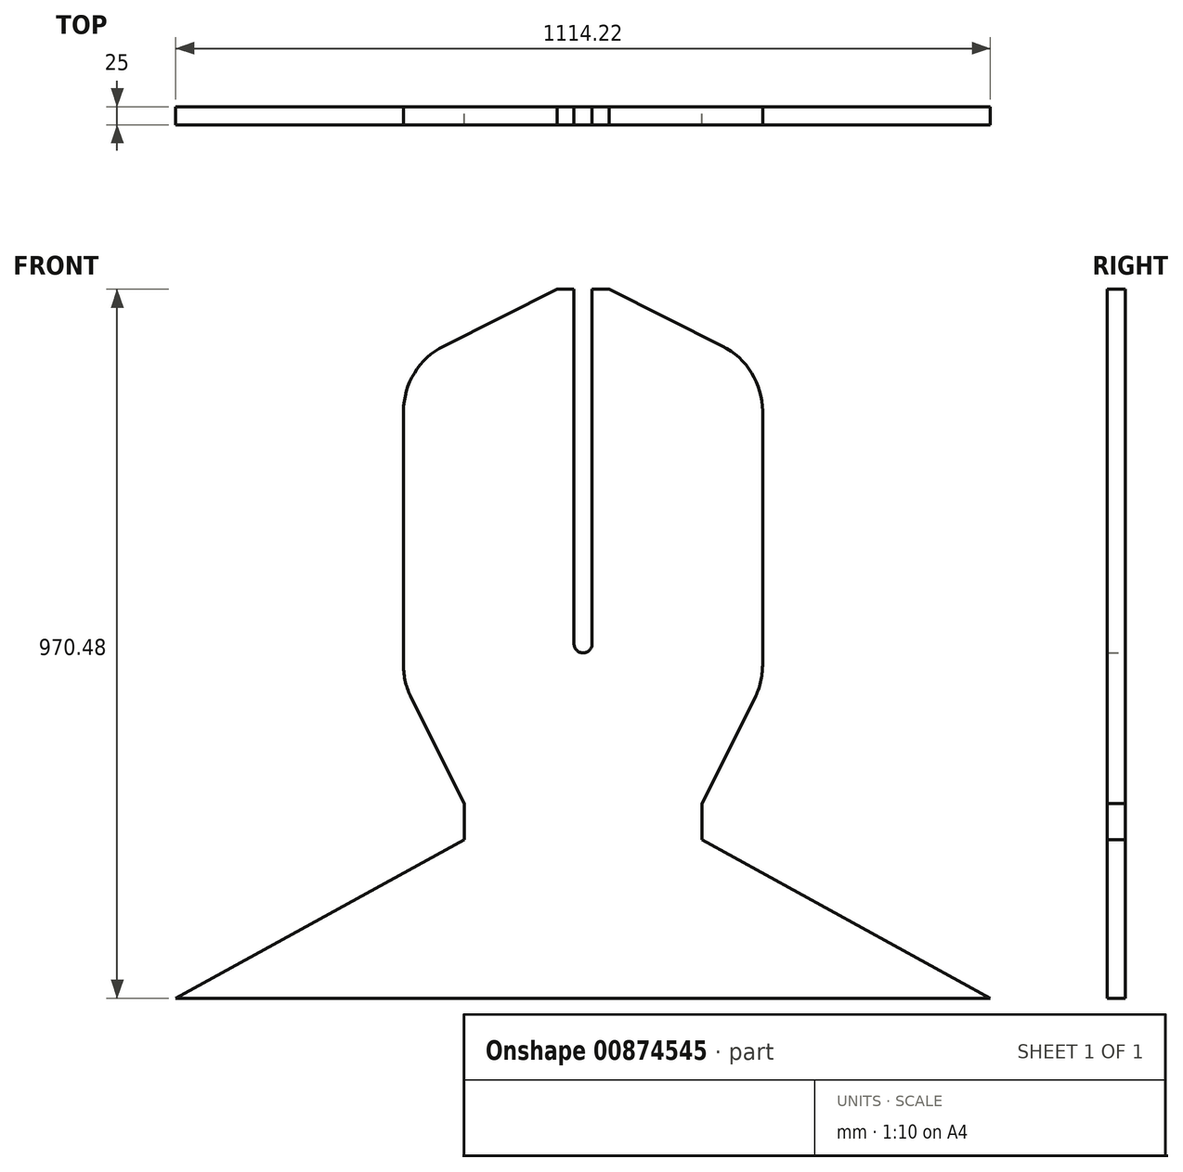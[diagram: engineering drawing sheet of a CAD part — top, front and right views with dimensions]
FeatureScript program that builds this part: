
annotation { "Feature Type Name" : "Feature", "Feature Type Description" : "" }
export const myFeature = defineFeature(function(context is Context, id is Id, definition is map)
    precondition{}
    {
        {
            var Q0;
            Q0=qCreatedBy(makeId("Front.planeOp"),FACE);
            var sketch = newSketch(context, id + "F0", { "sketchPlane" : qUnion([Q0])});
            skLineSegment(sketch, "E0", {"start": v(518.2, -507.34) * mm, "end": v(123.76, -290.72) * mm});
            skLineSegment(sketch, "E1", {"start": v(123.76, -290.72) * mm, "end": v(123.76, -240.72) * mm});
            skLineSegment(sketch, "E2", {"start": v(123.76, -240.72) * mm, "end": v(196.05, -96.48) * mm});
            skLineSegment(sketch, "E3", {"start": v(206.65, -51.68) * mm, "end": v(206.65, 296.08) * mm});
            skLineSegment(sketch, "E4", {"start": v(151.47, 385.47) * mm, "end": v(-3.42, 463.14) * mm});
            skLineSegment(sketch, "E5", {"start": v(-3.42, 463.14) * mm, "end": v(-26.42, 463.14) * mm});
            skLineSegment(sketch, "E6", {"start": v(-26.42, 463.14) * mm, "end": v(-26.42, -22.1) * mm});
            skLineSegment(sketch, "E7", {"start": v(-51.42, 463.14) * mm, "end": v(-51.42, -22.1) * mm});
            skPoint(sketch, "E8.orphan", {"position": v(-26.42, 463.14) * mm});
            skPoint(sketch, "E9.orphan", {"position": v(-51.42, 463.14) * mm});
            skPoint(sketch, "E10.visualSharp", {"position": v(206.65, 357.8) * mm});
            skArc(sketch, "E10.filletArc", {"start": v(206.65, 296.08) * mm, "mid": v(191.74, 348.6) * mm, "end": v(151.47, 385.47) * mm});
            skPoint(sketch, "E11.visualSharp", {"position": v(206.65, -75.33) * mm});
            skArc(sketch, "E11.filletArc", {"start": v(196.05, -96.48) * mm, "mid": v(203.96, -74.7) * mm, "end": v(206.65, -51.68) * mm});
            skLineSegment(sketch, "E12.trimOffspring", {"start": v(-51.42, 463.14) * mm, "end": v(-74.42, 463.14) * mm});
            skLineSegment(sketch, "E13", {"start": v(-51.42, 463.14) * mm, "end": v(-26.42, 463.14) * mm, "construction": true});
            skLineSegment(sketch, "E14", {"start": v(-38.92, 463.14) * mm, "end": v(-38.92, -507.34) * mm, "construction": true});
            skLineSegment(sketch, "E15.MirrorCS", {"start": v(-74.42, 463.14) * mm, "end": v(-51.42, 463.14) * mm});
            skLineSegment(sketch, "E16.MirrorCS", {"start": v(-229.31, 385.47) * mm, "end": v(-74.42, 463.14) * mm});
            skArc(sketch, "E17.MirrorCS", {"start": v(-284.5, 296.08) * mm, "mid": v(-269.59, 348.6) * mm, "end": v(-229.31, 385.47) * mm});
            skLineSegment(sketch, "E18.MirrorCS", {"start": v(-284.5, -51.68) * mm, "end": v(-284.5, 296.08) * mm});
            skLineSegment(sketch, "E19.MirrorCS", {"start": v(-201.6, -240.72) * mm, "end": v(-273.9, -96.48) * mm});
            skArc(sketch, "E20.MirrorCS", {"start": v(-273.9, -96.48) * mm, "mid": v(-281.8, -74.7) * mm, "end": v(-284.5, -51.68) * mm});
            skLineSegment(sketch, "E21.MirrorCS", {"start": v(-201.6, -290.72) * mm, "end": v(-201.6, -240.72) * mm});
            skLineSegment(sketch, "E22.MirrorCS", {"start": v(-596.03, -507.34) * mm, "end": v(-201.6, -290.72) * mm});
            skLineSegment(sketch, "E23", {"start": v(-596.03, -507.34) * mm, "end": v(518.2, -507.34) * mm});
            skArc(sketch, "E24", {"start": v(-51.42, -22.1) * mm, "mid": v(-38.92, -34.6) * mm, "end": v(-26.42, -22.1) * mm});
            skSolve(sketch);
        }
        {
            var Q0;
            Q0 = qSketchRegion(id + "F0", true);
            extrude(context, id + "F1", {"entities" : qUnion([Q0]), "depth" : 25 * mm, "offsetDistance" : 25 * mm});
        }
    });
